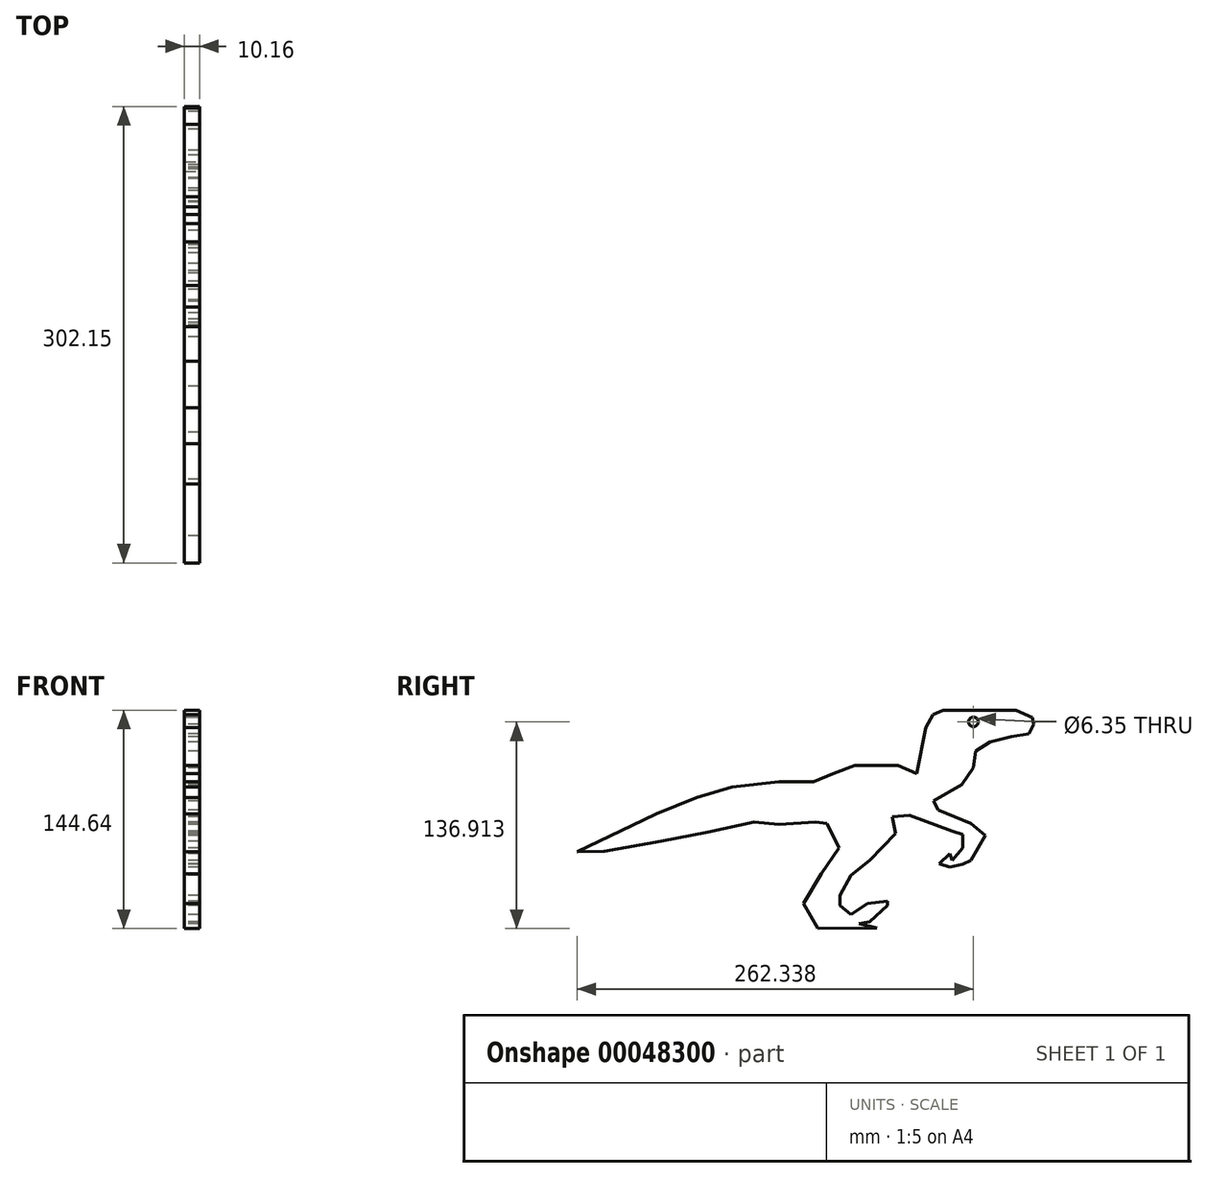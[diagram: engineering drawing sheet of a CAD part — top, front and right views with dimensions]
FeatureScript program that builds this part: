
annotation { "Feature Type Name" : "Feature", "Feature Type Description" : "" }
export const myFeature = defineFeature(function(context is Context, id is Id, definition is map)
    precondition{}
    {
        {
            var Q0;
            Q0=qCreatedBy(makeId("Right.planeOp"),FACE);
            var sketch = newSketch(context, id + "F0", { "sketchPlane" : qUnion([Q0])});
            skLineSegment(sketch, "E0", {"start": v(-103.97, 0) * mm, "end": v(-77.47, 10.77) * mm});
            skLineSegment(sketch, "E1", {"start": v(-77.47, 10.77) * mm, "end": v(-53.74, 17.94) * mm});
            skLineSegment(sketch, "E2", {"start": v(-53.74, 17.94) * mm, "end": v(-22.82, 21.25) * mm});
            skLineSegment(sketch, "E3", {"start": v(-22.82, 21.25) * mm, "end": v(0, 21.25) * mm});
            skLineSegment(sketch, "E4", {"start": v(0, 21.25) * mm, "end": v(13.06, 26.78) * mm});
            skLineSegment(sketch, "E5", {"start": v(13.06, 26.78) * mm, "end": v(27.42, 32.3) * mm});
            skLineSegment(sketch, "E6", {"start": v(27.42, 32.3) * mm, "end": v(39.01, 32.3) * mm});
            skLineSegment(sketch, "E7", {"start": v(39.01, 32.3) * mm, "end": v(56.12, 32.3) * mm});
            skLineSegment(sketch, "E8", {"start": v(56.12, 32.3) * mm, "end": v(68.27, 26.78) * mm});
            skLineSegment(sketch, "E9", {"start": v(68.27, 26.78) * mm, "end": v(74.34, 57.14) * mm});
            skLineSegment(sketch, "E10", {"start": v(74.34, 57.14) * mm, "end": v(79.31, 65.97) * mm});
            skLineSegment(sketch, "E11", {"start": v(79.31, 65.97) * mm, "end": v(85.94, 68.73) * mm});
            skLineSegment(sketch, "E12", {"start": v(85.94, 68.73) * mm, "end": v(134.02, 68.73) * mm});
            skLineSegment(sketch, "E13", {"start": v(134.02, 68.73) * mm, "end": v(144.95, 63.76) * mm});
            skLineSegment(sketch, "E14", {"start": v(144.95, 63.76) * mm, "end": v(145.74, 59.35) * mm});
            skLineSegment(sketch, "E15", {"start": v(145.74, 59.35) * mm, "end": v(142.61, 53.27) * mm});
            skLineSegment(sketch, "E16", {"start": v(142.61, 53.27) * mm, "end": v(130.9, 51.07) * mm});
            skLineSegment(sketch, "E17", {"start": v(130.9, 51.07) * mm, "end": v(116.85, 47.75) * mm});
            skLineSegment(sketch, "E18", {"start": v(116.85, 47.75) * mm, "end": v(107.48, 41.68) * mm});
            skLineSegment(sketch, "E19", {"start": v(107.48, 41.68) * mm, "end": v(105.92, 30.64) * mm});
            skLineSegment(sketch, "E20", {"start": v(105.92, 30.64) * mm, "end": v(98.11, 19.6) * mm});
            skLineSegment(sketch, "E21", {"start": v(98.11, 19.6) * mm, "end": v(79.37, 8.56) * mm});
            skLineSegment(sketch, "E22", {"start": v(79.37, 8.56) * mm, "end": v(82.5, 2.48) * mm});
            skLineSegment(sketch, "E23", {"start": v(82.5, 2.48) * mm, "end": v(104.36, -6.35) * mm});
            skLineSegment(sketch, "E24", {"start": v(104.36, -6.35) * mm, "end": v(113.73, -14.08) * mm});
            skLineSegment(sketch, "E25", {"start": v(113.73, -14.08) * mm, "end": v(104.36, -30.64) * mm});
            skLineSegment(sketch, "E26", {"start": v(104.36, -30.64) * mm, "end": v(98.9, -33.4) * mm});
            skLineSegment(sketch, "E27", {"start": v(98.9, -33.4) * mm, "end": v(90.3, -35.06) * mm});
            skLineSegment(sketch, "E28", {"start": v(90.3, -35.06) * mm, "end": v(83.28, -32.85) * mm});
            skLineSegment(sketch, "E29", {"start": v(83.28, -32.85) * mm, "end": v(90.3, -26.22) * mm});
            skLineSegment(sketch, "E30", {"start": v(90.3, -26.22) * mm, "end": v(91.86, -30.64) * mm});
            skLineSegment(sketch, "E31", {"start": v(91.86, -30.64) * mm, "end": v(98.9, -22.36) * mm});
            skLineSegment(sketch, "E32", {"start": v(98.9, -22.36) * mm, "end": v(98.9, -13.53) * mm});
            skLineSegment(sketch, "E33", {"start": v(98.9, -13.53) * mm, "end": v(91.86, -11.32) * mm});
            skLineSegment(sketch, "E34", {"start": v(91.86, -11.32) * mm, "end": v(63.76, -0.83) * mm});
            skLineSegment(sketch, "E35", {"start": v(63.76, -0.83) * mm, "end": v(52.05, -1.93) * mm});
            skLineSegment(sketch, "E36", {"start": v(52.05, -1.93) * mm, "end": v(54.39, -12.97) * mm});
            skLineSegment(sketch, "E37", {"start": v(54.39, -12.97) * mm, "end": v(37.21, -30.64) * mm});
            skLineSegment(sketch, "E38", {"start": v(37.21, -30.64) * mm, "end": v(24.72, -40.58) * mm});
            skLineSegment(sketch, "E39", {"start": v(24.72, -40.58) * mm, "end": v(17.7, -53.83) * mm});
            skLineSegment(sketch, "E40", {"start": v(17.7, -53.83) * mm, "end": v(17.7, -60.45) * mm});
            skLineSegment(sketch, "E41", {"start": v(17.7, -60.45) * mm, "end": v(24.72, -66.52) * mm});
            skLineSegment(sketch, "E42", {"start": v(24.72, -66.52) * mm, "end": v(35.65, -59.35) * mm});
            skLineSegment(sketch, "E43", {"start": v(35.65, -59.35) * mm, "end": v(48.92, -57.7) * mm});
            skLineSegment(sketch, "E44", {"start": v(48.92, -57.7) * mm, "end": v(48.92, -60.45) * mm});
            skLineSegment(sketch, "E45", {"start": v(48.92, -60.45) * mm, "end": v(37.21, -71.5) * mm});
            skLineSegment(sketch, "E46", {"start": v(37.21, -71.5) * mm, "end": v(30.19, -72.6) * mm});
            skLineSegment(sketch, "E47", {"start": v(30.19, -72.6) * mm, "end": v(41.9, -75.36) * mm});
            skLineSegment(sketch, "E48", {"start": v(41.9, -75.36) * mm, "end": v(2.86, -75.9) * mm});
            skLineSegment(sketch, "E49", {"start": v(2.86, -75.9) * mm, "end": v(-6.5, -59.35) * mm});
            skLineSegment(sketch, "E50", {"start": v(-6.5, -59.35) * mm, "end": v(5.2, -39.47) * mm});
            skLineSegment(sketch, "E51", {"start": v(5.2, -39.47) * mm, "end": v(16.91, -22.36) * mm});
            skLineSegment(sketch, "E52", {"start": v(16.91, -22.36) * mm, "end": v(9.1, -6.35) * mm});
            skLineSegment(sketch, "E53", {"start": v(9.1, -6.35) * mm, "end": v(1.3, -5.24) * mm});
            skLineSegment(sketch, "E54", {"start": v(1.3, -5.24) * mm, "end": v(-22.9, -6.9) * mm});
            skLineSegment(sketch, "E55", {"start": v(-22.9, -6.9) * mm, "end": v(-39.3, -5.24) * mm});
            skLineSegment(sketch, "E56", {"start": v(-39.3, -5.24) * mm, "end": v(-69.75, -11.87) * mm});
            skLineSegment(sketch, "E57", {"start": v(-69.75, -11.87) * mm, "end": v(-100.98, -17.94) * mm});
            skLineSegment(sketch, "E58", {"start": v(-100.98, -17.94) * mm, "end": v(-138.45, -24.57) * mm});
            skLineSegment(sketch, "E59", {"start": v(-138.45, -24.57) * mm, "end": v(-156.41, -25.12) * mm});
            skLineSegment(sketch, "E60", {"start": v(-156.41, -25.12) * mm, "end": v(-112.69, -4.14) * mm});
            skLineSegment(sketch, "E61", {"start": v(-112.69, -4.14) * mm, "end": v(-103.97, 0) * mm});
            skSolve(sketch);
        }
        {
            var Q0;
            Q0=makeQuery(id+"F0.imprint","IMPRINT",FACE,{"disambiguationData":[TD([[makeQuery(id+"F0.imprint","IMPRINT",EDGE,{"derivedFrom":sQuery(id+"F0.wireOp",EDGE,"E0")}),-1.0]])]});
            extrude(context, id + "F1", {"entities" : qUnion([Q0]), "depth" : 10.16 * mm});
        }
        {
            var Q0;
            Q0=makeQuery(id+"F1.opExtrude","CAP_FACE",FACE,{"disambiguationData":[OSD([sQuery(id+"F0.wireOp",EDGE,"E0"),sQuery(id+"F0.wireOp",EDGE,"E1"),sQuery(id+"F0.wireOp",EDGE,"E2"),sQuery(id+"F0.wireOp",EDGE,"E3"),sQuery(id+"F0.wireOp",EDGE,"E4"),sQuery(id+"F0.wireOp",EDGE,"E5"),sQuery(id+"F0.wireOp",EDGE,"E6"),sQuery(id+"F0.wireOp",EDGE,"E7"),sQuery(id+"F0.wireOp",EDGE,"E8"),sQuery(id+"F0.wireOp",EDGE,"E9"),sQuery(id+"F0.wireOp",EDGE,"E10"),sQuery(id+"F0.wireOp",EDGE,"E11"),sQuery(id+"F0.wireOp",EDGE,"E12"),sQuery(id+"F0.wireOp",EDGE,"E13"),sQuery(id+"F0.wireOp",EDGE,"E14"),sQuery(id+"F0.wireOp",EDGE,"E15"),sQuery(id+"F0.wireOp",EDGE,"E16"),sQuery(id+"F0.wireOp",EDGE,"E17"),sQuery(id+"F0.wireOp",EDGE,"E18"),sQuery(id+"F0.wireOp",EDGE,"E19"),sQuery(id+"F0.wireOp",EDGE,"E20"),sQuery(id+"F0.wireOp",EDGE,"E21"),sQuery(id+"F0.wireOp",EDGE,"E22"),sQuery(id+"F0.wireOp",EDGE,"E23"),sQuery(id+"F0.wireOp",EDGE,"E24"),sQuery(id+"F0.wireOp",EDGE,"E25"),sQuery(id+"F0.wireOp",EDGE,"E26"),sQuery(id+"F0.wireOp",EDGE,"E27"),sQuery(id+"F0.wireOp",EDGE,"E28"),sQuery(id+"F0.wireOp",EDGE,"E29"),sQuery(id+"F0.wireOp",EDGE,"E30"),sQuery(id+"F0.wireOp",EDGE,"E31"),sQuery(id+"F0.wireOp",EDGE,"E32"),sQuery(id+"F0.wireOp",EDGE,"E33"),sQuery(id+"F0.wireOp",EDGE,"E34"),sQuery(id+"F0.wireOp",EDGE,"E35"),sQuery(id+"F0.wireOp",EDGE,"E36"),sQuery(id+"F0.wireOp",EDGE,"E37"),sQuery(id+"F0.wireOp",EDGE,"E38"),sQuery(id+"F0.wireOp",EDGE,"E39"),sQuery(id+"F0.wireOp",EDGE,"E40"),sQuery(id+"F0.wireOp",EDGE,"E41"),sQuery(id+"F0.wireOp",EDGE,"E42"),sQuery(id+"F0.wireOp",EDGE,"E43"),sQuery(id+"F0.wireOp",EDGE,"E44"),sQuery(id+"F0.wireOp",EDGE,"E45"),sQuery(id+"F0.wireOp",EDGE,"E46"),sQuery(id+"F0.wireOp",EDGE,"E47"),sQuery(id+"F0.wireOp",EDGE,"E48"),sQuery(id+"F0.wireOp",EDGE,"E49"),sQuery(id+"F0.wireOp",EDGE,"E50"),sQuery(id+"F0.wireOp",EDGE,"E51"),sQuery(id+"F0.wireOp",EDGE,"E52"),sQuery(id+"F0.wireOp",EDGE,"E53"),sQuery(id+"F0.wireOp",EDGE,"E54"),sQuery(id+"F0.wireOp",EDGE,"E55"),sQuery(id+"F0.wireOp",EDGE,"E56"),sQuery(id+"F0.wireOp",EDGE,"E57"),sQuery(id+"F0.wireOp",EDGE,"E58"),sQuery(id+"F0.wireOp",EDGE,"E59"),sQuery(id+"F0.wireOp",EDGE,"E60"),sQuery(id+"F0.wireOp",EDGE,"E61")])],"isStart":false});
            var sketch = newSketch(context, id + "F2", { "sketchPlane" : qUnion([Q0])});
            skCircle(sketch, "E62", {"center": v(105.93, 61) * mm, "radius": 4.24 * mm});
            skSolve(sketch);
        }
        {
            var Q0;
            Q0=sQuery(id+"F2.wireOp",VERTEX,"E62.center");
            var Q1;
            Q1=makeQuery(id+"F1.opExtrude","SWEPT_BODY",BODY,{"disambiguationData":[OSD([sQuery(id+"F0.wireOp",EDGE,"E0"),sQuery(id+"F0.wireOp",EDGE,"E1"),sQuery(id+"F0.wireOp",EDGE,"E2"),sQuery(id+"F0.wireOp",EDGE,"E3"),sQuery(id+"F0.wireOp",EDGE,"E4"),sQuery(id+"F0.wireOp",EDGE,"E5"),sQuery(id+"F0.wireOp",EDGE,"E6"),sQuery(id+"F0.wireOp",EDGE,"E7"),sQuery(id+"F0.wireOp",EDGE,"E8"),sQuery(id+"F0.wireOp",EDGE,"E9"),sQuery(id+"F0.wireOp",EDGE,"E10"),sQuery(id+"F0.wireOp",EDGE,"E11"),sQuery(id+"F0.wireOp",EDGE,"E12"),sQuery(id+"F0.wireOp",EDGE,"E13"),sQuery(id+"F0.wireOp",EDGE,"E14"),sQuery(id+"F0.wireOp",EDGE,"E15"),sQuery(id+"F0.wireOp",EDGE,"E16"),sQuery(id+"F0.wireOp",EDGE,"E17"),sQuery(id+"F0.wireOp",EDGE,"E18"),sQuery(id+"F0.wireOp",EDGE,"E19"),sQuery(id+"F0.wireOp",EDGE,"E20"),sQuery(id+"F0.wireOp",EDGE,"E21"),sQuery(id+"F0.wireOp",EDGE,"E22"),sQuery(id+"F0.wireOp",EDGE,"E23"),sQuery(id+"F0.wireOp",EDGE,"E24"),sQuery(id+"F0.wireOp",EDGE,"E25"),sQuery(id+"F0.wireOp",EDGE,"E26"),sQuery(id+"F0.wireOp",EDGE,"E27"),sQuery(id+"F0.wireOp",EDGE,"E28"),sQuery(id+"F0.wireOp",EDGE,"E29"),sQuery(id+"F0.wireOp",EDGE,"E30"),sQuery(id+"F0.wireOp",EDGE,"E31"),sQuery(id+"F0.wireOp",EDGE,"E32"),sQuery(id+"F0.wireOp",EDGE,"E33"),sQuery(id+"F0.wireOp",EDGE,"E34"),sQuery(id+"F0.wireOp",EDGE,"E35"),sQuery(id+"F0.wireOp",EDGE,"E36"),sQuery(id+"F0.wireOp",EDGE,"E37"),sQuery(id+"F0.wireOp",EDGE,"E38"),sQuery(id+"F0.wireOp",EDGE,"E39"),sQuery(id+"F0.wireOp",EDGE,"E40"),sQuery(id+"F0.wireOp",EDGE,"E41"),sQuery(id+"F0.wireOp",EDGE,"E42"),sQuery(id+"F0.wireOp",EDGE,"E43"),sQuery(id+"F0.wireOp",EDGE,"E44"),sQuery(id+"F0.wireOp",EDGE,"E45"),sQuery(id+"F0.wireOp",EDGE,"E46"),sQuery(id+"F0.wireOp",EDGE,"E47"),sQuery(id+"F0.wireOp",EDGE,"E48"),sQuery(id+"F0.wireOp",EDGE,"E49"),sQuery(id+"F0.wireOp",EDGE,"E50"),sQuery(id+"F0.wireOp",EDGE,"E51"),sQuery(id+"F0.wireOp",EDGE,"E52"),sQuery(id+"F0.wireOp",EDGE,"E53"),sQuery(id+"F0.wireOp",EDGE,"E54"),sQuery(id+"F0.wireOp",EDGE,"E55"),sQuery(id+"F0.wireOp",EDGE,"E56"),sQuery(id+"F0.wireOp",EDGE,"E57"),sQuery(id+"F0.wireOp",EDGE,"E58"),sQuery(id+"F0.wireOp",EDGE,"E59"),sQuery(id+"F0.wireOp",EDGE,"E60"),sQuery(id+"F0.wireOp",EDGE,"E61")])]});
            hole(context, id + "F3", {"style" : HoleStyle.SIMPLE, "holeDiameter" : 6.35 * mm, "endStyle" : HoleEndStyle.THROUGH, "locations" : qUnion([Q0]), "scope" : qUnion([Q1])});
        }
    });
